FCSTD DOCUMENT  (FreeCAD 0.20R29410 (Git))
Label: Chamber1
License: All rights reserved
LicenseURL: http://en.wikipedia.org/wiki/All_rights_reserved
objects: Sketcher::SketchObject×1, PartDesign::Body×1
note: 2 computed .brp shape members not serialized (recipe doc carries the construction recipe); baked Part::Feature solids carry a one-line shape summary decoded from their .brp

FEATURE [Sketcher::SketchObject] Sketch
  FullyConstrained = false
  MapMode = 5
  Support = -> [XY_Plane]
  expr: .Constraints.ChamberScrewHolderOuter = .Constraints.ChamberScrew + 10mm
  expr: .Constraints.OuterChamber = .Constraints.InnerChamber + 20mm
  expr: Constraints[5] = .Constraints.InnerChamber + .Constraints.ChamberScrewHolderOuter
  sketch-geometry (16):
    g0: ArcOfCircle CenterX=-49.9793 CenterY=43.5579 CenterZ=0 NormalX=0 NormalY=0 NormalZ=1 AngleXU=0 Radius=100 StartAngle=1.47698 EndAngle=3.02439
    g1: ArcOfCircle CenterX=-49.9793 CenterY=43.5579 CenterZ=0 NormalX=0 NormalY=0 NormalZ=1 AngleXU=0 Radius=120 StartAngle=2.39708 EndAngle=3.04415
    g2: Circle CenterX=-120.688 CenterY=135.516 CenterZ=0 NormalX=0 NormalY=0 NormalZ=1 AngleXU=0 Radius=6
    g3: ArcOfCircle CenterX=-120.688 CenterY=135.516 CenterZ=0 NormalX=0 NormalY=0 NormalZ=1 AngleXU=0 Radius=16 StartAngle=5.3679 EndAngle=5.3679
    g4: ArcOfCircle CenterX=-120.688 CenterY=135.516 CenterZ=0 NormalX=0 NormalY=0 NormalZ=1 AngleXU=0 Radius=16 StartAngle=1.07013 EndAngle=3.36099
    g5: ArcOfCircle CenterX=-144.113 CenterY=130.292 CenterZ=0 NormalX=0 NormalY=0 NormalZ=1 AngleXU=0 Radius=8 StartAngle=5.53868 EndAngle=6.50259
    g6: ArcOfCircle CenterX=-109.168 CenterY=156.57 CenterZ=0 NormalX=0 NormalY=0 NormalZ=1 AngleXU=0 Radius=8 StartAngle=4.21172 EndAngle=4.87715
    g7: ArcOfCircle CenterX=-120.688 CenterY=135.516 CenterZ=0 NormalX=0 NormalY=0 NormalZ=1 AngleXU=0 Radius=16 StartAngle=5.3679 EndAngle=5.3679
    g8: ArcOfCircle CenterX=-120.688 CenterY=135.516 CenterZ=0 NormalX=0 NormalY=0 NormalZ=1 AngleXU=0 Radius=16 StartAngle=1.07013 EndAngle=3.36099
    g9: ArcOfCircle CenterX=-120.688 CenterY=135.516 CenterZ=0 NormalX=0 NormalY=0 NormalZ=1 AngleXU=0 Radius=16 StartAngle=1.07013 EndAngle=3.36099
    g10: ArcOfCircle CenterX=-120.688 CenterY=135.516 CenterZ=0 NormalX=0 NormalY=0 NormalZ=1 AngleXU=0 Radius=16 StartAngle=5.3679 EndAngle=5.3679
    g11: ArcOfCircle CenterX=-49.9793 CenterY=43.5579 CenterZ=0 NormalX=0 NormalY=0 NormalZ=1 AngleXU=0 Radius=120 StartAngle=1.49389 EndAngle=2.07408
    g12: ArcOfCircle CenterX=-120.688 CenterY=135.516 CenterZ=0 NormalX=0 NormalY=0 NormalZ=1 AngleXU=0 Radius=16 StartAngle=5.3679 EndAngle=5.3679
    g13: ArcOfCircle CenterX=-120.688 CenterY=135.516 CenterZ=0 NormalX=0 NormalY=0 NormalZ=1 AngleXU=0 Radius=16 StartAngle=1.07013 EndAngle=3.36099
    g14: ArcOfCircle CenterX=-120.688 CenterY=135.516 CenterZ=0 NormalX=0 NormalY=0 NormalZ=1 AngleXU=0 Radius=16 StartAngle=5.3679 EndAngle=5.3679
    g15: ArcOfCircle CenterX=-120.688 CenterY=135.516 CenterZ=0 NormalX=0 NormalY=0 NormalZ=1 AngleXU=0 Radius=16 StartAngle=1.07013 EndAngle=3.36099
  constraints (50):
    c: Coincident(g1,g0)
    c: Radius(g1) = 120  'OuterChamber'
    c: Coincident(g3,g2)
    c: Radius(g2) = 6  'ChamberScrew'
    c: Radius(g3) = 16  'ChamberScrewHolderOuter'
    c: Distance(g0,g2) = 116
    c: PointOnObject(g3,g0)
    c: Equal(g3,g4)
    c: PointOnObject(g7,g0)
    c: Coincident(g3,g4)
    c: Tangent(g4,g5) = 1.5708
    c: Tangent(g1,g5) = 1.5708
    c: Tangent(g4,g6) = 1.5708
    c: Coincident(g11,g6) = 1.5708
    c: Equal(g3,g7)
    c: PointOnObject(g8,g5)
    c: PointOnObject(g7,g0)
    c: Coincident(g3,g7)
    c: Equal(g3,g8)
    c: PointOnObject(g12,g0)
    c: PointOnObject(g8,g6)
    c: Coincident(g3,g8)
    c: Radius(g5) = 8
    c: Radius(g6) = 8
    c: Equal(g3,g9)
    c: PointOnObject(g14,g0)
    c: PointOnObject(g9,g6)
    c: Coincident(g3,g9)
    c: Equal(g9,g10)
    c: PointOnObject(g9,g5)
    c: PointOnObject(g10,g0)
    c: Coincident(g9,g10)
    c: Equal(g1,g11)
    c: Coincident(g1,g11)
    c: Equal(g10,g12)
    c: PointOnObject(g13,g5)
    c: PointOnObject(g12,g0)
    c: Coincident(g10,g12)
    c: Equal(g10,g13)
    c: PointOnObject(g10,g0)
    c: PointOnObject(g13,g6)
    c: Coincident(g10,g13)
    c: Equal(g3,g14)
    c: PointOnObject(g15,g5)
    c: PointOnObject(g14,g0)
    c: Coincident(g3,g14)
    c: Equal(g3,g15)
    c: PointOnObject(g3,g0)
    c: PointOnObject(g15,g6)
    c: Coincident(g3,g15)
FEATURE [PartDesign::Body] Body
  Group = -> [Sketch]
  Origin = -> Origin
